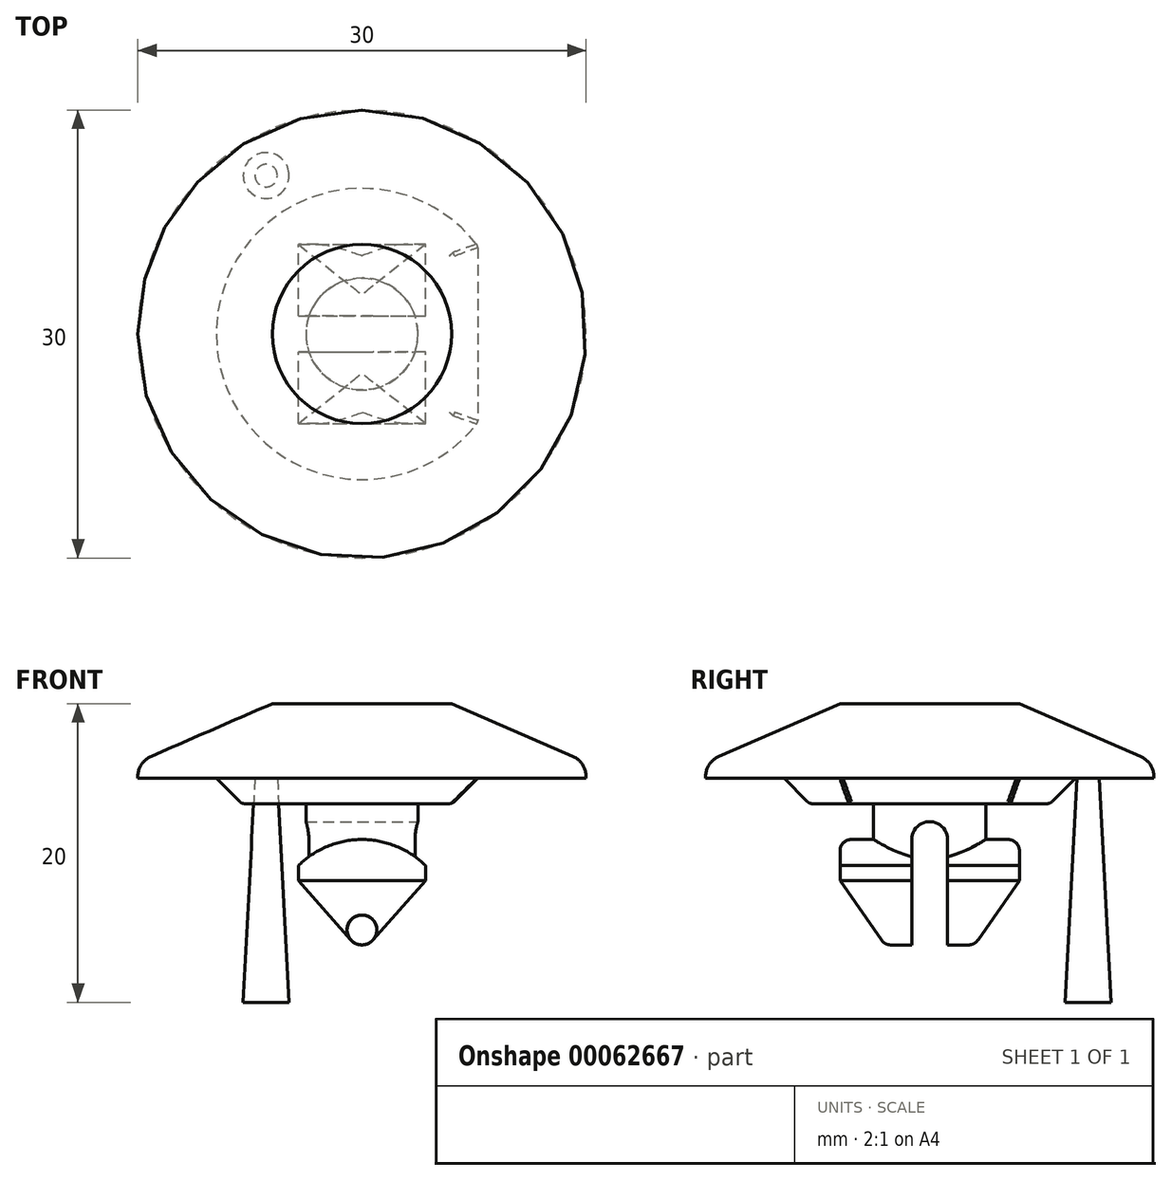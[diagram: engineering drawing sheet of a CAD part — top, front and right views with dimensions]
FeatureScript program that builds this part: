
annotation { "Feature Type Name" : "Feature", "Feature Type Description" : "" }
export const myFeature = defineFeature(function(context is Context, id is Id, definition is map)
    precondition{}
    {
        {
            var Q0;
            Q0=qCreatedBy(makeId("Front.planeOp"),FACE);
            var sketch = newSketch(context, id + "F0", { "sketchPlane" : qUnion([Q0])});
            skLineSegment(sketch, "E0", {"start": v(0, 0) * mm, "end": v(0, 45) * mm});
            skLineSegment(sketch, "E1", {"start": v(0, 45) * mm, "end": v(-15, 45) * mm});
            skLineSegment(sketch, "E2", {"start": v(0, 0) * mm, "end": v(-8, 0) * mm});
            skFitSpline(sketch, "E3", {"points": [v(-15, 45) * mm, v(-9.89, 31.85) * mm, v(-7.97, 5.04) * mm], "startDerivative": vector(-0.53, -36.4) * mm, "endDerivative": vector(-0.2, -58.1) * mm});
            skLineSegment(sketch, "E4.MirrorCS", {"start": v(0, -45) * mm, "end": v(-15, -45) * mm});
            skLineSegment(sketch, "E5.MirrorCS", {"start": v(0, 0) * mm, "end": v(0, -45) * mm});
            skFitSpline(sketch, "E6.MirrorCS", {"points": [v(-15, -45) * mm, v(-9.89, -31.85) * mm, v(-7.97, -5.04) * mm], "startDerivative": vector(-0.53, 36.4) * mm, "endDerivative": vector(-0.2, 58.1) * mm});
            skEllipticalArc(sketch, "E7", {});
            skPoint(sketch, "E8.MirrorCS.start.orphan", {"position": v(-8, 0) * mm});
            skPoint(sketch, "E9.visualSharp", {"position": v(-8, 20.72) * mm});
            skArc(sketch, "E9.filletArc", {"start": v(-9, 17.6) * mm, "mid": v(-8.3, 21.6) * mm, "end": v(-8.41, 25.67) * mm});
            skPoint(sketch, "E10.visualSharp", {"position": v(-8, -20.72) * mm});
            skArc(sketch, "E10.filletArc", {"start": v(-8.41, -25.67) * mm, "mid": v(-8.3, -21.6) * mm, "end": v(-9, -17.6) * mm});
            const initialGuessF0  = {"E7": [0.0066548618488013744, 0, 0, 1, 0.03582403436303139, 0.017969114314154242, 1.0572183333888945, 2.0843743202008995]};
            skSetInitialGuess(sketch, initialGuessF0);
            skSolve(sketch);
        }
        {
            var Q0;
            Q0=qSketchRegion(id+"F0",true);
            var Q1;
            Q1=sQuery(id+"F0.wireOp",EDGE,"E5.MirrorCS");
            revolve(context, id + "F1", {"entities" : qUnion([Q0]), "axis" : qUnion([Q1]), "revolveType" : RevolveType.FULL});
        }
        {
            var Q0;
            Q0=makeQuery(id+"F1.opRevolve","SWEPT_FACE",FACE,{"disambiguationData":[OSD([sQuery(id+"F0.wireOp",EDGE,"E4.MirrorCS")])]});
            var sketch = newSketch(context, id + "F2", { "sketchPlane" : qUnion([Q0])});
            skCircle(sketch, "E11", {"center": v(0, 0) * mm, "radius": 4 * mm});
            skSolve(sketch);
        }
        {
            var Q0;
            Q0=qSketchRegion(id+"F2",true);
            extrude(context, id + "F3", {"entities" : qUnion([Q0]), "operationType" : NewBodyOperationType.REMOVE, "oppositeDirection" : true, "depth" : 10 * mm});
        }
        {
            var Q0;
            Q0=qCreatedBy(makeId("Front.planeOp"),FACE);
            var sketch = newSketch(context, id + "F4", { "sketchPlane" : qUnion([Q0])});
            skLineSegment(sketch, "E12", {"start": v(0, 0) * mm, "end": v(0, 35) * mm});
            skArc(sketch, "E13", {"start": v(5.66, 33) * mm, "mid": v(0, 41) * mm, "end": v(-5.66, 33) * mm});
            skArc(sketch, "E14", {"start": v(-2.83, 25) * mm, "mid": v(0, 23) * mm, "end": v(2.83, 25) * mm});
            skLineSegment(sketch, "E15", {"start": v(5.66, 33) * mm, "end": v(2.83, 25) * mm});
            skLineSegment(sketch, "E16", {"start": v(-2.83, 25) * mm, "end": v(-5.66, 33) * mm});
            skLineSegment(sketch, "E17.MirrorCS", {"start": v(5.66, -33) * mm, "end": v(2.83, -25) * mm});
            skLineSegment(sketch, "E18.MirrorCS", {"start": v(0, 0) * mm, "end": v(0, -35) * mm});
            skLineSegment(sketch, "E19.MirrorCS", {"start": v(-2.83, -25) * mm, "end": v(-5.66, -33) * mm});
            skArc(sketch, "E20.MirrorCS", {"start": v(5.66, -33) * mm, "mid": v(0, -41) * mm, "end": v(-5.66, -33) * mm});
            skArc(sketch, "E21.MirrorCS", {"start": v(-2.83, -25) * mm, "mid": v(0, -23) * mm, "end": v(2.83, -25) * mm});
            skLineSegment(sketch, "E22", {"start": v(2, 16.6) * mm, "end": v(2, -16.6) * mm});
            skPoint(sketch, "E22.startSnap0", {"position": v(0, 17.5) * mm});
            skPoint(sketch, "E22.endSnap0", {"position": v(0, -17.5) * mm});
            skFitSpline(sketch, "E23", {"points": [v(2, 18) * mm, v(6.5, 0) * mm, v(2, -18) * mm], "startDerivative": vector(24, 0) * mm, "endDerivative": vector(-24, 0) * mm});
            skArc(sketch, "E24.filletArc", {"start": v(3.67, 17.34) * mm, "mid": v(2.6, 17.51) * mm, "end": v(2, 16.6) * mm});
            skArc(sketch, "E25.filletArc", {"start": v(2, -16.6) * mm, "mid": v(2.6, -17.51) * mm, "end": v(3.67, -17.34) * mm});
            skArc(sketch, "E26.MirrorCS", {"start": v(-3.67, 17.34) * mm, "mid": v(-2.6, 17.51) * mm, "end": v(-2, 16.6) * mm});
            skArc(sketch, "E27.MirrorCS", {"start": v(-2, -16.6) * mm, "mid": v(-2.6, -17.51) * mm, "end": v(-3.67, -17.34) * mm});
            skPoint(sketch, "E28.MirrorP", {"position": v(-2, 18) * mm});
            skLineSegment(sketch, "E29.MirrorCS", {"start": v(-2, 16.6) * mm, "end": v(-2, -16.6) * mm});
            skFitSpline(sketch, "E30.MirrorCS", {"points": [v(-2, 18) * mm, v(-6.5, 0) * mm, v(-2, -18) * mm], "startDerivative": vector(-24, 0) * mm, "endDerivative": vector(24, 0) * mm});
            skSolve(sketch);
        }
        {
            var Q0;
            Q0=qSketchRegion(id+"F4",true);
            extrude(context, id + "F5", {"entities" : qUnion([Q0]), "operationType" : NewBodyOperationType.REMOVE, "endBound" : BoundingType.THROUGH_ALL, "oppositeDirection" : true, "depth" : 25 * mm, "hasSecondDirection" : true, "secondDirectionOppositeDirection" : false, "secondDirectionDepth" : 25 * mm});
        }
        {
            var Q0;
            Q0=makeQuery(id+"F1.opRevolve","SWEPT_FACE",FACE,{"disambiguationData":[OSD([sQuery(id+"F0.wireOp",EDGE,"E1")])]});
            var sketch = newSketch(context, id + "F6", { "sketchPlane" : qUnion([Q0])});
            skCircle(sketch, "E31", {"center": v(0, 0) * mm, "radius": 4 * mm});
            skSolve(sketch);
        }
        {
            var Q0;
            Q0=qSketchRegion(id+"F6",true);
            extrude(context, id + "F7", {"entities" : qUnion([Q0]), "operationType" : NewBodyOperationType.REMOVE, "oppositeDirection" : true, "depth" : 10 * mm});
        }
        {
            var Q0;
            Q0=makeQuery(id+"F1.opRevolve","SWEPT_FACE",FACE,{"disambiguationData":[OSD([sQuery(id+"F0.wireOp",EDGE,"E4.MirrorCS")])]});
            var sketch = newSketch(context, id + "F8", { "sketchPlane" : qUnion([Q0])});
            skArc(sketch, "E32", {"start": v(-8, -6) * mm, "mid": v(10, 0) * mm, "end": v(-8, 6) * mm});
            skLineSegment(sketch, "E33", {"start": v(-8, -6) * mm, "end": v(-8, 6) * mm});
            skSolve(sketch);
        }
        {
            var Q0;
            Q0=qSketchRegion(id+"F8",true);
            extrude(context, id + "F9", {"entities" : qUnion([Q0]), "operationType" : NewBodyOperationType.REMOVE, "oppositeDirection" : true, "depth" : 2 * mm, "hasDraft" : true, "draftAngle" : 45 * degree, "draftPullDirection" : true});
        }
        {
            var Q0;
            Q0=makeQuery(id+"F1.opRevolve","SWEPT_FACE",FACE,{"disambiguationData":[OSD([sQuery(id+"F0.wireOp",EDGE,"E1")])]});
            var sketch = newSketch(context, id + "F10", { "sketchPlane" : qUnion([Q0])});
            skArc(sketch, "E34", {"start": v(8, 6) * mm, "mid": v(-10, 0) * mm, "end": v(8, -6) * mm});
            skLineSegment(sketch, "E35", {"start": v(8, 6) * mm, "end": v(8, -6) * mm});
            skSolve(sketch);
        }
        {
            var Q0;
            Q0=qSketchRegion(id+"F10",true);
            extrude(context, id + "F11", {"entities" : qUnion([Q0]), "operationType" : NewBodyOperationType.REMOVE, "oppositeDirection" : true, "depth" : 2 * mm, "hasDraft" : true, "draftAngle" : 45 * degree, "draftPullDirection" : true});
        }
        {
            var Q0;
            Q0=makeQuery(id+"F9.boolean.opBoolean","COPY",EDGE,{"derivedFrom":makeQuery(id+"F9.opExtrude","CAP_EDGE",EDGE,{"disambiguationData":[OSD([sQuery(id+"F8.wireOp",EDGE,"E32")])],"isStart":true})});
            var Q1;
            Q1=makeQuery(id+"F9.boolean.opBoolean","INTERSECT",EDGE,{"derivedFrom":[makeQuery(id+"F3.boolean.opBoolean","COPY",FACE,{"derivedFrom":makeQuery(id+"F3.opExtrude","SWEPT_FACE",FACE,{"disambiguationData":[OSD([sQuery(id+"F2.wireOp",EDGE,"E11")])]})}),makeQuery(id+"F9.opExtrude","CAP_FACE",FACE,{"disambiguationData":[OSD([sQuery(id+"F8.wireOp",EDGE,"E32")])],"isStart":false})]});
            var Q2;
            Q2=makeQuery(id+"F11.boolean.opBoolean","COPY",EDGE,{"derivedFrom":makeQuery(id+"F11.opExtrude","CAP_EDGE",EDGE,{"disambiguationData":[OSD([sQuery(id+"F10.wireOp",EDGE,"E34")])],"isStart":true})});
            var Q3;
            Q3=makeQuery(id+"F11.boolean.opBoolean","INTERSECT",EDGE,{"derivedFrom":[makeQuery(id+"F7.boolean.opBoolean","COPY",FACE,{"derivedFrom":makeQuery(id+"F7.opExtrude","SWEPT_FACE",FACE,{"disambiguationData":[OSD([sQuery(id+"F6.wireOp",EDGE,"E31")])]})}),makeQuery(id+"F11.opExtrude","CAP_FACE",FACE,{"disambiguationData":[OSD([sQuery(id+"F10.wireOp",EDGE,"E34")])],"isStart":false})]});
            var Q4;
            Q4=makeQuery(id+"F11.boolean.opBoolean","COPY",EDGE,{"derivedFrom":makeQuery(id+"F11.opExtrude","CAP_EDGE",EDGE,{"disambiguationData":[OSD([sQuery(id+"F10.wireOp",EDGE,"E35")])],"isStart":true})});
            var Q5;
            Q5=makeQuery(id+"F9.boolean.opBoolean","COPY",EDGE,{"derivedFrom":makeQuery(id+"F9.opExtrude","CAP_EDGE",EDGE,{"disambiguationData":[OSD([sQuery(id+"F8.wireOp",EDGE,"E33")])],"isStart":true})});
            fillet(context, id + "F12", {"entities" : qUnion([Q0, Q1, Q2, Q3, Q4, Q5]), "radius" : .5 * mm, "tangentPropagation" : true, "allowEdgeOverflow" : false});
        }
        {
            var Q0;
            Q0=makeQuery(id+"F5.boolean.opBoolean","INTERSECT",EDGE,{"disambiguationData":[OD(1.0)],"derivedFrom":[makeQuery(id+"F1.opRevolve","SWEPT_FACE",FACE,{"disambiguationData":[OSD([sQuery(id+"F0.wireOp",EDGE,"E3")])]}),makeQuery(id+"F5.opExtrude","SWEPT_FACE",FACE,{"disambiguationData":[OSD([sQuery(id+"F4.wireOp",EDGE,"E13")])]})]});
            var Q1;
            Q1=makeQuery(id+"F5.boolean.opBoolean","INTERSECT",EDGE,{"disambiguationData":[OD(1.0)],"derivedFrom":[makeQuery(id+"F1.opRevolve","SWEPT_FACE",FACE,{"disambiguationData":[OSD([sQuery(id+"F0.wireOp",EDGE,"E3")])]}),makeQuery(id+"F5.opExtrude","SWEPT_FACE",FACE,{"disambiguationData":[OSD([sQuery(id+"F4.wireOp",EDGE,"E16")])]})]});
            var Q2;
            Q2=makeQuery(id+"F5.boolean.opBoolean","INTERSECT",EDGE,{"disambiguationData":[OD(1.0)],"derivedFrom":[makeQuery(id+"F1.opRevolve","SWEPT_FACE",FACE,{"disambiguationData":[OSD([sQuery(id+"F0.wireOp",EDGE,"E3")])]}),makeQuery(id+"F5.opExtrude","SWEPT_FACE",FACE,{"disambiguationData":[OSD([sQuery(id+"F4.wireOp",EDGE,"E15")])]})]});
            var Q3;
            Q3=makeQuery(id+"F5.boolean.opBoolean","INTERSECT",EDGE,{"disambiguationData":[OD(1.0)],"derivedFrom":[makeQuery(id+"F1.opRevolve","SWEPT_FACE",FACE,{"disambiguationData":[OSD([sQuery(id+"F0.wireOp",EDGE,"E9.filletArc")])]}),makeQuery(id+"F5.opExtrude","SWEPT_FACE",FACE,{"disambiguationData":[OSD([sQuery(id+"F4.wireOp",EDGE,"E14")])]})]});
            var Q4;
            Q4=makeQuery(id+"F5.boolean.opBoolean","INTERSECT",EDGE,{"disambiguationData":[OD(1.0)],"derivedFrom":[makeQuery(id+"F1.opRevolve","SWEPT_FACE",FACE,{"disambiguationData":[OSD([sQuery(id+"F0.wireOp",EDGE,"E9.filletArc")])]}),makeQuery(id+"F5.opExtrude","SWEPT_FACE",FACE,{"disambiguationData":[OSD([sQuery(id+"F4.wireOp",EDGE,"E16")])]})]});
            var Q5;
            Q5=makeQuery(id+"F5.boolean.opBoolean","INTERSECT",EDGE,{"disambiguationData":[OD(1.0)],"derivedFrom":[makeQuery(id+"F1.opRevolve","SWEPT_FACE",FACE,{"disambiguationData":[OSD([sQuery(id+"F0.wireOp",EDGE,"E9.filletArc")])]}),makeQuery(id+"F5.opExtrude","SWEPT_FACE",FACE,{"disambiguationData":[OSD([sQuery(id+"F4.wireOp",EDGE,"E15")])]})]});
            var Q6;
            Q6=makeQuery(id+"F5.boolean.opBoolean","INTERSECT",EDGE,{"disambiguationData":[OD(0.0)],"derivedFrom":[makeQuery(id+"F1.opRevolve","SWEPT_FACE",FACE,{"disambiguationData":[OSD([sQuery(id+"F0.wireOp",EDGE,"E3")])]}),makeQuery(id+"F5.opExtrude","SWEPT_FACE",FACE,{"disambiguationData":[OSD([sQuery(id+"F4.wireOp",EDGE,"E13")])]})]});
            var Q7;
            Q7=makeQuery(id+"F5.boolean.opBoolean","INTERSECT",EDGE,{"disambiguationData":[OD(0.0)],"derivedFrom":[makeQuery(id+"F1.opRevolve","SWEPT_FACE",FACE,{"disambiguationData":[OSD([sQuery(id+"F0.wireOp",EDGE,"E3")])]}),makeQuery(id+"F5.opExtrude","SWEPT_FACE",FACE,{"disambiguationData":[OSD([sQuery(id+"F4.wireOp",EDGE,"E15")])]})]});
            var Q8;
            Q8=makeQuery(id+"F5.boolean.opBoolean","INTERSECT",EDGE,{"disambiguationData":[OD(0.0)],"derivedFrom":[makeQuery(id+"F1.opRevolve","SWEPT_FACE",FACE,{"disambiguationData":[OSD([sQuery(id+"F0.wireOp",EDGE,"E3")])]}),makeQuery(id+"F5.opExtrude","SWEPT_FACE",FACE,{"disambiguationData":[OSD([sQuery(id+"F4.wireOp",EDGE,"E16")])]})]});
            var Q9;
            Q9=makeQuery(id+"F5.boolean.opBoolean","INTERSECT",EDGE,{"disambiguationData":[OD(0.0)],"derivedFrom":[makeQuery(id+"F1.opRevolve","SWEPT_FACE",FACE,{"disambiguationData":[OSD([sQuery(id+"F0.wireOp",EDGE,"E9.filletArc")])]}),makeQuery(id+"F5.opExtrude","SWEPT_FACE",FACE,{"disambiguationData":[OSD([sQuery(id+"F4.wireOp",EDGE,"E14")])]})]});
            var Q10;
            Q10=makeQuery(id+"F5.boolean.opBoolean","INTERSECT",EDGE,{"disambiguationData":[OD(0.0)],"derivedFrom":[makeQuery(id+"F1.opRevolve","SWEPT_FACE",FACE,{"disambiguationData":[OSD([sQuery(id+"F0.wireOp",EDGE,"E9.filletArc")])]}),makeQuery(id+"F5.opExtrude","SWEPT_FACE",FACE,{"disambiguationData":[OSD([sQuery(id+"F4.wireOp",EDGE,"E16")])]})]});
            var Q11;
            Q11=makeQuery(id+"F5.boolean.opBoolean","INTERSECT",EDGE,{"disambiguationData":[OD(0.0)],"derivedFrom":[makeQuery(id+"F1.opRevolve","SWEPT_FACE",FACE,{"disambiguationData":[OSD([sQuery(id+"F0.wireOp",EDGE,"E9.filletArc")])]}),makeQuery(id+"F5.opExtrude","SWEPT_FACE",FACE,{"disambiguationData":[OSD([sQuery(id+"F4.wireOp",EDGE,"E15")])]})]});
            var Q12;
            Q12=makeQuery(id+"F5.boolean.opBoolean","INTERSECT",EDGE,{"disambiguationData":[OD(0.0)],"derivedFrom":[makeQuery(id+"F1.opRevolve","SWEPT_FACE",FACE,{"disambiguationData":[OSD([sQuery(id+"F0.wireOp",EDGE,"E6.MirrorCS")])]}),makeQuery(id+"F5.opExtrude","SWEPT_FACE",FACE,{"disambiguationData":[OSD([sQuery(id+"F4.wireOp",EDGE,"E20.MirrorCS")])]})]});
            var Q13;
            Q13=makeQuery(id+"F5.boolean.opBoolean","INTERSECT",EDGE,{"disambiguationData":[OD(0.0)],"derivedFrom":[makeQuery(id+"F1.opRevolve","SWEPT_FACE",FACE,{"disambiguationData":[OSD([sQuery(id+"F0.wireOp",EDGE,"E6.MirrorCS")])]}),makeQuery(id+"F5.opExtrude","SWEPT_FACE",FACE,{"disambiguationData":[OSD([sQuery(id+"F4.wireOp",EDGE,"E19.MirrorCS")])]})]});
            var Q14;
            Q14=makeQuery(id+"F5.boolean.opBoolean","INTERSECT",EDGE,{"disambiguationData":[OD(0.0)],"derivedFrom":[makeQuery(id+"F1.opRevolve","SWEPT_FACE",FACE,{"disambiguationData":[OSD([sQuery(id+"F0.wireOp",EDGE,"E10.filletArc")])]}),makeQuery(id+"F5.opExtrude","SWEPT_FACE",FACE,{"disambiguationData":[OSD([sQuery(id+"F4.wireOp",EDGE,"E19.MirrorCS")])]})]});
            var Q15;
            Q15=makeQuery(id+"F5.boolean.opBoolean","INTERSECT",EDGE,{"disambiguationData":[OD(0.0)],"derivedFrom":[makeQuery(id+"F1.opRevolve","SWEPT_FACE",FACE,{"disambiguationData":[OSD([sQuery(id+"F0.wireOp",EDGE,"E10.filletArc")])]}),makeQuery(id+"F5.opExtrude","SWEPT_FACE",FACE,{"disambiguationData":[OSD([sQuery(id+"F4.wireOp",EDGE,"E21.MirrorCS")])]})]});
            var Q16;
            Q16=makeQuery(id+"F5.boolean.opBoolean","INTERSECT",EDGE,{"disambiguationData":[OD(0.0)],"derivedFrom":[makeQuery(id+"F1.opRevolve","SWEPT_FACE",FACE,{"disambiguationData":[OSD([sQuery(id+"F0.wireOp",EDGE,"E10.filletArc")])]}),makeQuery(id+"F5.opExtrude","SWEPT_FACE",FACE,{"disambiguationData":[OSD([sQuery(id+"F4.wireOp",EDGE,"E17.MirrorCS")])]})]});
            var Q17;
            Q17=makeQuery(id+"F5.boolean.opBoolean","INTERSECT",EDGE,{"disambiguationData":[OD(0.0)],"derivedFrom":[makeQuery(id+"F1.opRevolve","SWEPT_FACE",FACE,{"disambiguationData":[OSD([sQuery(id+"F0.wireOp",EDGE,"E6.MirrorCS")])]}),makeQuery(id+"F5.opExtrude","SWEPT_FACE",FACE,{"disambiguationData":[OSD([sQuery(id+"F4.wireOp",EDGE,"E17.MirrorCS")])]})]});
            var Q18;
            Q18=makeQuery(id+"F5.boolean.opBoolean","INTERSECT",EDGE,{"disambiguationData":[OD(1.0)],"derivedFrom":[makeQuery(id+"F1.opRevolve","SWEPT_FACE",FACE,{"disambiguationData":[OSD([sQuery(id+"F0.wireOp",EDGE,"E6.MirrorCS")])]}),makeQuery(id+"F5.opExtrude","SWEPT_FACE",FACE,{"disambiguationData":[OSD([sQuery(id+"F4.wireOp",EDGE,"E20.MirrorCS")])]})]});
            var Q19;
            Q19=makeQuery(id+"F5.boolean.opBoolean","INTERSECT",EDGE,{"disambiguationData":[OD(1.0)],"derivedFrom":[makeQuery(id+"F1.opRevolve","SWEPT_FACE",FACE,{"disambiguationData":[OSD([sQuery(id+"F0.wireOp",EDGE,"E6.MirrorCS")])]}),makeQuery(id+"F5.opExtrude","SWEPT_FACE",FACE,{"disambiguationData":[OSD([sQuery(id+"F4.wireOp",EDGE,"E17.MirrorCS")])]})]});
            var Q20;
            Q20=makeQuery(id+"F5.boolean.opBoolean","INTERSECT",EDGE,{"disambiguationData":[OD(1.0)],"derivedFrom":[makeQuery(id+"F1.opRevolve","SWEPT_FACE",FACE,{"disambiguationData":[OSD([sQuery(id+"F0.wireOp",EDGE,"E10.filletArc")])]}),makeQuery(id+"F5.opExtrude","SWEPT_FACE",FACE,{"disambiguationData":[OSD([sQuery(id+"F4.wireOp",EDGE,"E17.MirrorCS")])]})]});
            var Q21;
            Q21=makeQuery(id+"F5.boolean.opBoolean","INTERSECT",EDGE,{"disambiguationData":[OD(1.0)],"derivedFrom":[makeQuery(id+"F1.opRevolve","SWEPT_FACE",FACE,{"disambiguationData":[OSD([sQuery(id+"F0.wireOp",EDGE,"E10.filletArc")])]}),makeQuery(id+"F5.opExtrude","SWEPT_FACE",FACE,{"disambiguationData":[OSD([sQuery(id+"F4.wireOp",EDGE,"E21.MirrorCS")])]})]});
            var Q22;
            Q22=makeQuery(id+"F5.boolean.opBoolean","INTERSECT",EDGE,{"disambiguationData":[OD(1.0)],"derivedFrom":[makeQuery(id+"F1.opRevolve","SWEPT_FACE",FACE,{"disambiguationData":[OSD([sQuery(id+"F0.wireOp",EDGE,"E10.filletArc")])]}),makeQuery(id+"F5.opExtrude","SWEPT_FACE",FACE,{"disambiguationData":[OSD([sQuery(id+"F4.wireOp",EDGE,"E19.MirrorCS")])]})]});
            var Q23;
            Q23=makeQuery(id+"F5.boolean.opBoolean","INTERSECT",EDGE,{"disambiguationData":[OD(1.0)],"derivedFrom":[makeQuery(id+"F1.opRevolve","SWEPT_FACE",FACE,{"disambiguationData":[OSD([sQuery(id+"F0.wireOp",EDGE,"E6.MirrorCS")])]}),makeQuery(id+"F5.opExtrude","SWEPT_FACE",FACE,{"disambiguationData":[OSD([sQuery(id+"F4.wireOp",EDGE,"E19.MirrorCS")])]})]});
            fillet(context, id + "F13", {"entities" : qUnion([Q0, Q1, Q2, Q3, Q4, Q5, Q6, Q7, Q8, Q9, Q10, Q11, Q12, Q13, Q14, Q15, Q16, Q17, Q18, Q19, Q20, Q21, Q22, Q23]), "radius" : 1 * mm, "tangentPropagation" : true, "allowEdgeOverflow" : false});
        }
        {
            var Q0;
            Q0=makeQuery(id+"F5.boolean.opBoolean","INTERSECT",EDGE,{"disambiguationData":[OD(1.0)],"derivedFrom":[makeQuery(id+"F1.opRevolve","SWEPT_FACE",FACE,{"disambiguationData":[OSD([sQuery(id+"F0.wireOp",EDGE,"E7")])]}),makeQuery(id+"F5.opExtrude","SWEPT_FACE",FACE,{"disambiguationData":[OSD([sQuery(id+"F4.wireOp",EDGE,"E23")])]})]});
            var Q1;
            Q1=makeQuery(id+"F5.boolean.opBoolean","INTERSECT",EDGE,{"disambiguationData":[OD(0.0)],"derivedFrom":[makeQuery(id+"F1.opRevolve","SWEPT_FACE",FACE,{"disambiguationData":[OSD([sQuery(id+"F0.wireOp",EDGE,"E7")])]}),makeQuery(id+"F5.opExtrude","SWEPT_FACE",FACE,{"disambiguationData":[OSD([sQuery(id+"F4.wireOp",EDGE,"E23")])]})]});
            var Q2;
            Q2=makeQuery(id+"F5.boolean.opBoolean","INTERSECT",EDGE,{"disambiguationData":[OD(0.0)],"derivedFrom":[makeQuery(id+"F1.opRevolve","SWEPT_FACE",FACE,{"disambiguationData":[OSD([sQuery(id+"F0.wireOp",EDGE,"E7")])]}),makeQuery(id+"F5.opExtrude","SWEPT_FACE",FACE,{"disambiguationData":[OSD([sQuery(id+"F4.wireOp",EDGE,"E30.MirrorCS")])]})]});
            var Q3;
            Q3=makeQuery(id+"F5.boolean.opBoolean","INTERSECT",EDGE,{"disambiguationData":[OD(1.0)],"derivedFrom":[makeQuery(id+"F1.opRevolve","SWEPT_FACE",FACE,{"disambiguationData":[OSD([sQuery(id+"F0.wireOp",EDGE,"E7")])]}),makeQuery(id+"F5.opExtrude","SWEPT_FACE",FACE,{"disambiguationData":[OSD([sQuery(id+"F4.wireOp",EDGE,"E30.MirrorCS")])]})]});
            fillet(context, id + "F14", {"entities" : qUnion([Q0, Q1, Q2, Q3]), "radius" : 1.5 * mm, "tangentPropagation" : true, "allowEdgeOverflow" : false});
        }
        {
            var Q0;
            Q0=makeQuery(id+"F9.boolean.opBoolean","COPY",FACE,{"derivedFrom":makeQuery(id+"F9.opExtrude","CAP_FACE",FACE,{"disambiguationData":[OSD([sQuery(id+"F8.wireOp",EDGE,"E32")])],"isStart":false})});
            var sketch = newSketch(context, id + "F15", { "sketchPlane" : qUnion([Q0])});
            skCircle(sketch, "E36", {"center": v(0, 0) * mm, "radius": 4 * mm});
            skSolve(sketch);
        }
        {
            var Q0;
            Q0=qSketchRegion(id+"F15",true);
            extrude(context, id + "F16", {"entities" : qUnion([Q0]), "operationType" : NewBodyOperationType.REMOVE, "endBound" : BoundingType.THROUGH_ALL, "oppositeDirection" : true, "depth" : 25 * mm});
        }
        {
            var Q0;
            Q0=qCreatedBy(makeId("Front.planeOp"),FACE);
            var sketch = newSketch(context, id + "F17", { "sketchPlane" : qUnion([Q0])});
            skLineSegment(sketch, "E37.0", {"start": v(0, 45) * mm, "end": v(15, 45) * mm});
            skArc(sketch, "E38", {"start": v(15, 45) * mm, "mid": v(14.78, 45.88) * mm, "end": v(14.1, 46.48) * mm});
            skLineSegment(sketch, "E39", {"start": v(0, 45) * mm, "end": v(0, 50) * mm});
            skLineSegment(sketch, "E40", {"start": v(0, 50) * mm, "end": v(6, 50) * mm});
            skLineSegment(sketch, "E41", {"start": v(14.1, 46.48) * mm, "end": v(6, 50) * mm});
            skLineSegment(sketch, "E42", {"start": v(0, 45) * mm, "end": v(0, 43.3) * mm});
            skLineSegment(sketch, "E43", {"start": v(0, 43.3) * mm, "end": v(7.84, 43.3) * mm});
            skLineSegment(sketch, "E44", {"start": v(8.2, 43.45) * mm, "end": v(9.75, 45) * mm});
            skLineSegment(sketch, "E45", {"start": v(0, 0) * mm, "end": v(0, 43.3) * mm});
            skLineSegment(sketch, "E46.bottom", {"start": v(0, 43.3) * mm, "end": v(3.75, 43.3) * mm});
            skLineSegment(sketch, "E46.top", {"start": v(0, 39.6) * mm, "end": v(3.75, 39.6) * mm});
            skLineSegment(sketch, "E46.left", {"start": v(0, 43.3) * mm, "end": v(0, 39.6) * mm});
            skLineSegment(sketch, "E46.right", {"start": v(3.75, 43.3) * mm, "end": v(3.75, 39.6) * mm});
            skPoint(sketch, "E47.visualSharp", {"position": v(8.05, 43.3) * mm});
            skArc(sketch, "E47.filletArc", {"start": v(7.84, 43.3) * mm, "mid": v(8.03, 43.34) * mm, "end": v(8.2, 43.45) * mm});
            skSolve(sketch);
        }
        {
            var Q0;
            Q0 = qSketchRegion(id + "F17", true);
            var Q1;
            Q1=sQuery(id+"F17.wireOp",EDGE,"E45");
            revolve(context, id + "F18", {"entities" : qUnion([Q0]), "axis" : qUnion([Q1]), "revolveType" : RevolveType.FULL});
        }
        {
            var Q0;
            Q0=makeQuery(id+"F18.opRevolve","SWEPT_FACE",FACE,{"disambiguationData":[OSD([sQuery(id+"F17.wireOp",EDGE,"E37.0")])]});
            var sketch = newSketch(context, id + "F19", { "sketchPlane" : qUnion([Q0])});
            skArc(sketch, "E48.0", {"start": v(7.75, -5.92) * mm, "mid": v(9.75, 0) * mm, "end": v(7.75, 5.92) * mm});
            skLineSegment(sketch, "E49", {"start": v(7.75, 5.92) * mm, "end": v(7.75, -5.92) * mm});
            skSolve(sketch);
        }
        {
            var Q0;
            Q0 = qSketchRegion(id + "F19", true);
            extrude(context, id + "F20", {"entities" : qUnion([Q0]), "operationType" : NewBodyOperationType.REMOVE, "depth" : 2 * mm, "hasDraft" : true, "draftAngle" : 45 * degree});
        }
        {
            var Q0;
            Q0=makeQuery(id+"F20.boolean.opBoolean","INTERSECT",EDGE,{"derivedFrom":[makeQuery(id+"F18.opRevolve","SWEPT_FACE",FACE,{"disambiguationData":[OSD([sQuery(id+"F17.wireOp",EDGE,"E43")])]}),makeQuery(id+"F20.opExtrude","SWEPT_FACE",FACE,{"disambiguationData":[OSD([sQuery(id+"F19.wireOp",EDGE,"E49")])]})]});
            fillet(context, id + "F21", {"entities" : qUnion([Q0]), "radius" : .5 * mm, "tangentPropagation" : true, "allowEdgeOverflow" : false});
        }
        {
            var Q0;
            Q0=qCreatedBy(makeId("Front.planeOp"),FACE);
            var sketch = newSketch(context, id + "F22", { "sketchPlane" : qUnion([Q0])});
            skArc(sketch, "E50", {"start": v(4.25, 39.16) * mm, "mid": v(0, 40.9) * mm, "end": v(-4.25, 39.16) * mm});
            skLineSegment(sketch, "E51.bottom", {"start": v(-4.25, 39.16) * mm, "end": v(4.25, 39.16) * mm});
            skPoint(sketch, "E52.0.end.orphan", {"position": v(-3.75, 39.6) * mm});
            skPoint(sketch, "E52.0.start.orphan", {"position": v(3.75, 39.6) * mm});
            skLineSegment(sketch, "E53.top", {"start": v(-4.25, 38.16) * mm, "end": v(4.25, 38.16) * mm});
            skLineSegment(sketch, "E53.left", {"start": v(-4.25, 39.16) * mm, "end": v(-4.25, 38.16) * mm});
            skLineSegment(sketch, "E53.right", {"start": v(4.25, 39.16) * mm, "end": v(4.25, 38.16) * mm});
            skCircle(sketch, "E54", {"center": v(0, 34.84) * mm, "radius": 1 * mm});
            skLineSegment(sketch, "E55", {"start": v(-4.25, 38.16) * mm, "end": v(-0.75, 34.18) * mm});
            skLineSegment(sketch, "E56", {"start": v(0, 40.9) * mm, "end": v(0, 33.84) * mm});
            skLineSegment(sketch, "E57", {"start": v(4.25, 38.16) * mm, "end": v(0.75, 34.18) * mm});
            skSolve(sketch);
        }
        {
            var Q0;
            Q0 = qSketchRegion(id + "F22", true);
            extrude(context, id + "F23", {"entities" : qUnion([Q0]), "operationType" : NewBodyOperationType.ADD, "depth" : 6 * mm, "hasSecondDirection" : true, "secondDirectionOppositeDirection" : true, "secondDirectionDepth" : 6 * mm});
        }
        {
            var Q0;
            Q0=qCreatedBy(makeId("Right.planeOp"),FACE);
            var sketch = newSketch(context, id + "F24", { "sketchPlane" : qUnion([Q0])});
            skLineSegment(sketch, "E58.0", {"start": v(6, 33.84) * mm, "end": v(6, 34.18) * mm});
            skLineSegment(sketch, "E59.0", {"start": v(-6, 33.84) * mm, "end": v(-6, 34.18) * mm});
            skLineSegment(sketch, "E60", {"start": v(-2.6, 33.84) * mm, "end": v(-1.2, 33.84) * mm});
            skLineSegment(sketch, "E61", {"start": v(-6, 38.16) * mm, "end": v(-3.22, 34.16) * mm});
            skLineSegment(sketch, "E62", {"start": v(6, 38.16) * mm, "end": v(3.22, 34.16) * mm});
            skLineSegment(sketch, "E63.right", {"start": v(1.2, 33.84) * mm, "end": v(1.2, 40.9) * mm});
            skLineSegment(sketch, "E64.right", {"start": v(-1.2, 40.9) * mm, "end": v(-1.2, 33.84) * mm});
            skArc(sketch, "E65", {"start": v(1.2, 40.9) * mm, "mid": v(0, 42.1) * mm, "end": v(-1.2, 40.9) * mm});
            skPoint(sketch, "E66.visualSharp", {"position": v(-6, 40.9) * mm});
            skArc(sketch, "E66.filletArc", {"start": v(-5.25, 40.9) * mm, "mid": v(-5.78, 40.68) * mm, "end": v(-6, 40.15) * mm});
            skPoint(sketch, "E67.visualSharp", {"position": v(6, 40.9) * mm});
            skArc(sketch, "E67.filletArc", {"start": v(6, 40.15) * mm, "mid": v(5.78, 40.68) * mm, "end": v(5.25, 40.9) * mm});
            skPoint(sketch, "E68.newPointA", {"position": v(-6, 33.84) * mm});
            skPoint(sketch, "E68.newPointB", {"position": v(-3, 33.84) * mm});
            skArc(sketch, "E68.filletArc", {"start": v(-3.22, 34.16) * mm, "mid": v(-2.96, 33.93) * mm, "end": v(-2.6, 33.84) * mm});
            skPoint(sketch, "E69.newPointA", {"position": v(5.5, 33.84) * mm});
            skPoint(sketch, "E69.newPointB", {"position": v(3, 33.84) * mm});
            skArc(sketch, "E69.filletArc", {"start": v(2.6, 33.84) * mm, "mid": v(2.96, 33.93) * mm, "end": v(3.22, 34.16) * mm});
            skLineSegment(sketch, "E70", {"start": v(5.25, 40.9) * mm, "end": v(6, 40.9) * mm});
            skLineSegment(sketch, "E71", {"start": v(6, 40.9) * mm, "end": v(6, 40.15) * mm});
            skLineSegment(sketch, "E72", {"start": v(-5.25, 40.9) * mm, "end": v(-6, 40.9) * mm});
            skLineSegment(sketch, "E73", {"start": v(-6, 40.9) * mm, "end": v(-6, 40.15) * mm});
            skLineSegment(sketch, "E74", {"start": v(-6, 38.16) * mm, "end": v(-6, 33.22) * mm});
            skLineSegment(sketch, "E75", {"start": v(-6, 33.22) * mm, "end": v(-1.72, 33.22) * mm});
            skLineSegment(sketch, "E76", {"start": v(0.7, 33.2) * mm, "end": v(6, 33.2) * mm});
            skLineSegment(sketch, "E77", {"start": v(6, 33.2) * mm, "end": v(6, 38.16) * mm});
            skLineSegment(sketch, "E78.trimOffspring", {"start": v(1.2, 33.84) * mm, "end": v(2.6, 33.84) * mm});
            skPoint(sketch, "E63.left.start.orphan", {"position": v(-0.25, 33.84) * mm});
            skPoint(sketch, "E79.0.start.orphan", {"position": v(6, 39.16) * mm});
            skPoint(sketch, "E80.0.start.orphan", {"position": v(-6, 39.16) * mm});
            skLineSegment(sketch, "E81", {"start": v(-1.72, 33.22) * mm, "end": v(0.7, 33.2) * mm});
            skSolve(sketch);
        }
        {
            var Q0;
            Q0 = qSketchRegion(id + "F24", true);
            extrude(context, id + "F25", {"entities" : qUnion([Q0]), "operationType" : NewBodyOperationType.REMOVE, "oppositeDirection" : true, "depth" : 5 * mm, "hasSecondDirection" : true, "secondDirectionOppositeDirection" : false, "secondDirectionDepth" : 5 * mm});
        }
        {
            var Q0;
            Q0=makeQuery(id+"F1.opRevolve","SWEPT_BODY",BODY,{"disambiguationData":[OSD([sQuery(id+"F0.wireOp",EDGE,"E0"),sQuery(id+"F0.wireOp",EDGE,"E1"),sQuery(id+"F0.wireOp",EDGE,"E3"),sQuery(id+"F0.wireOp",EDGE,"E4.MirrorCS"),sQuery(id+"F0.wireOp",EDGE,"E5.MirrorCS"),sQuery(id+"F0.wireOp",EDGE,"E6.MirrorCS"),sQuery(id+"F0.wireOp",EDGE,"E7"),sQuery(id+"F0.wireOp",EDGE,"E9.filletArc"),sQuery(id+"F0.wireOp",EDGE,"E10.filletArc")])]});
            deleteBodies(context, id + "F26", {"entities" : qUnion([Q0])});
        }
        {
            var Q0;
            Q0=makeQuery(id+"F20.boolean.opBoolean","MERGE",FACE,{"derivedFrom":[makeQuery(id+"F18.opRevolve","SWEPT_FACE",FACE,{"disambiguationData":[OSD([sQuery(id+"F17.wireOp",EDGE,"E37.0")])]}),makeQuery(id+"F20.opExtrude","CAP_FACE",FACE,{"disambiguationData":[OSD([sQuery(id+"F19.wireOp",EDGE,"E48.0"),sQuery(id+"F19.wireOp",EDGE,"E49")])],"isStart":true})]});
            var sketch = newSketch(context, id + "F27", { "sketchPlane" : qUnion([Q0])});
            skCircle(sketch, "E82", {"center": v(-6.4, -10.6) * mm, "radius": 0.75 * mm});
            skSolve(sketch);
        }
        {
            var Q0;
            Q0=makeQuery(id+"F27.imprint","IMPRINT",FACE,{"disambiguationData":[TD([[makeQuery(id+"F27.imprint","IMPRINT",EDGE,{"derivedFrom":sQuery(id+"F27.wireOp",EDGE,"E82")}),1.0]])]});
            extrude(context, id + "F28", {"entities" : qUnion([Q0]), "operationType" : NewBodyOperationType.ADD, "depth" : 15 * mm, "hasDraft" : true, "draftAngle" : 3 * degree});
        }
    });
